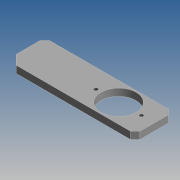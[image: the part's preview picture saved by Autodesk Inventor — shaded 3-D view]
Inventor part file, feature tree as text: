
AUTODESK INVENTOR PART (.ipt)
format: ipt  version: 2019 (Build 230136000, 136)  size: 218,112 bytes
history: native  units: mm
features: sketch x3, hole x2, chamfer x2, extrude x1
ambient origin geometry x8: Origin, YZ Plane, XZ Plane, XY Plane, X Axis, Y Axis, Z Axis, Center Point
bodies: Solid1 (feature_tree)
feature tree (8):
  extrude  "Extrusion1"  Depth=16.0mm
  hole  "Hole1"  [1 undecoded]
  chamfer  "Chamfer2"  Distance=2.0mm Angle=45.0deg
  chamfer  "Chamfer3"  Distance=4.0mm Angle=45.0deg
  hole  "Hole2"  [1 undecoded]
  sketch  "Sketch1"  dims[d0=54.0mm d1=16.0mm]
  sketch  "Sketch2"  dims[d2=3.0mm d3=0.0mm d4=12.0mm]
  sketch  "Sketch3"  dims[d5=14.7mm d6=6.0mm d7=4.0mm d8=2.0mm d9=90.0deg d10=8.0mm d11=20.594885mm d15=2.0mm d16=2.0mm d17=45.0deg d18=4.0mm d19=2.0mm d20=45.0deg d21=9.53mm d22=9.53mm d23=1.567mm d24=4.0mm d25=4.0mm d26=2.0mm d27=90.0deg d28=6.3mm d29=20.594885mm]
note: 2 required parameter values undecoded (feature->parameter linkage not recoverable at this tier; creation-order binding heuristic only, values carry confidence <= 0.55)
